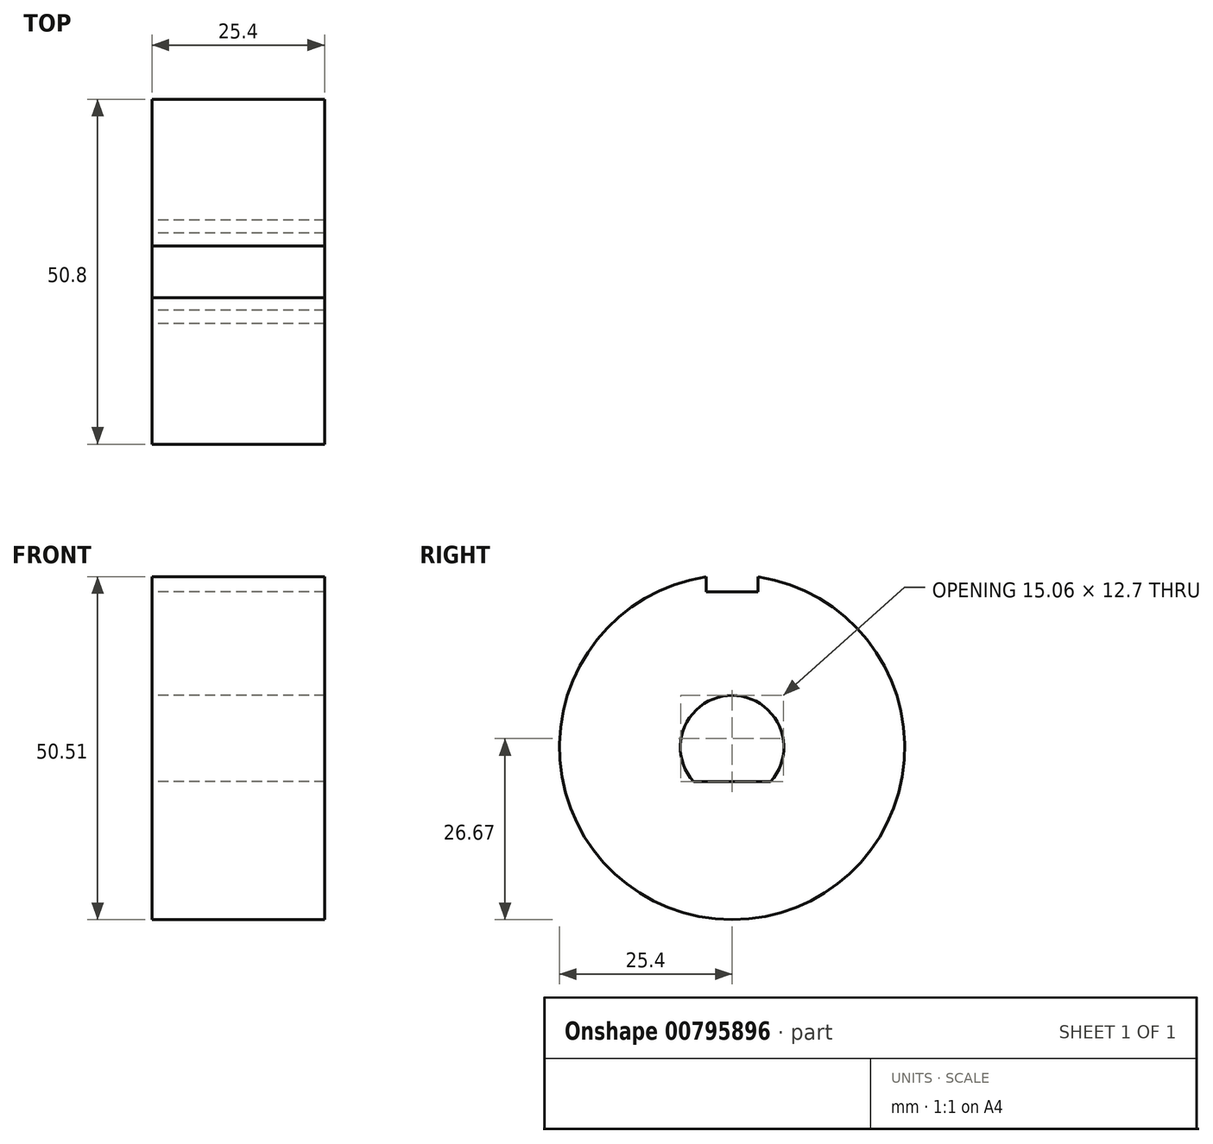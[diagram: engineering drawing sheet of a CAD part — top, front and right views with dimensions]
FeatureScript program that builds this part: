
annotation { "Feature Type Name" : "Feature", "Feature Type Description" : "" }
export const myFeature = defineFeature(function(context is Context, id is Id, definition is map)
    precondition{}
    {
        {
            var Q0;
            Q0=qCreatedBy(makeId("Right.planeOp"),FACE);
            var sketch = newSketch(context, id + "F0", { "sketchPlane" : qUnion([Q0])});
            skArc(sketch, "E0", {"start": v(5.68, -5.08) * mm, "mid": v(0, 7.62) * mm, "end": v(-5.68, -5.08) * mm});
            skLineSegment(sketch, "E1", {"start": v(-5.68, -5.08) * mm, "end": v(5.68, -5.08) * mm});
            skArc(sketch, "E2", {"start": v(-3.8, 25.11) * mm, "mid": v(0, -25.4) * mm, "end": v(3.81, 25.11) * mm});
            skLineSegment(sketch, "E3.top", {"start": v(3.81, 22.86) * mm, "end": v(-3.8, 22.86) * mm});
            skLineSegment(sketch, "E3.left", {"start": v(3.81, 25.11) * mm, "end": v(3.81, 22.86) * mm});
            skLineSegment(sketch, "E3.right", {"start": v(-3.8, 25.11) * mm, "end": v(-3.8, 22.86) * mm});
            skPoint(sketch, "E3.middle", {"position": v(0, 25.4) * mm});
            skPoint(sketch, "E3.bottom.end.orphan", {"position": v(-3.8, 27.94) * mm});
            skPoint(sketch, "E4.orphan", {"position": v(3.81, 27.94) * mm});
            skSolve(sketch);
        }
        {
            var Q0;
            Q0=makeQuery(id+"F0.imprint","IMPRINT",FACE,{"disambiguationData":[TD([[makeQuery(id+"F0.imprint","IMPRINT",EDGE,{"derivedFrom":sQuery(id+"F0.wireOp",EDGE,"E0")}),-1.0]])]});
            extrude(context, id + "F1", {"entities" : qUnion([Q0]), "depth" : 25.4 * mm, "offsetDistance" : 25.4 * mm});
        }
    });
